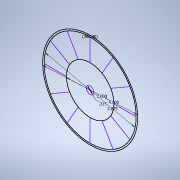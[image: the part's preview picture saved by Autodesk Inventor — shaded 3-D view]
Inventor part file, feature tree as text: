
AUTODESK INVENTOR PART (.ipt)
format: ipt  version: 2021 (Build 250183000, 183)  size: 99,328 bytes
history: native  units: in
note: dims shown in document units (in); Inventor stores cm internally (conversion verified against a paired STEP export)
features: sketch x1
ambient origin geometry x8: Origin, YZ Plane, XZ Plane, XY Plane, X Axis, Y Axis, Z Axis, Center Point
feature tree (1):
  sketch  "Sketch1"  dims[d0=3.875in d1=2.0in d2=4.7244in d4=360.0deg d6=4.0in d7=0.315in]
